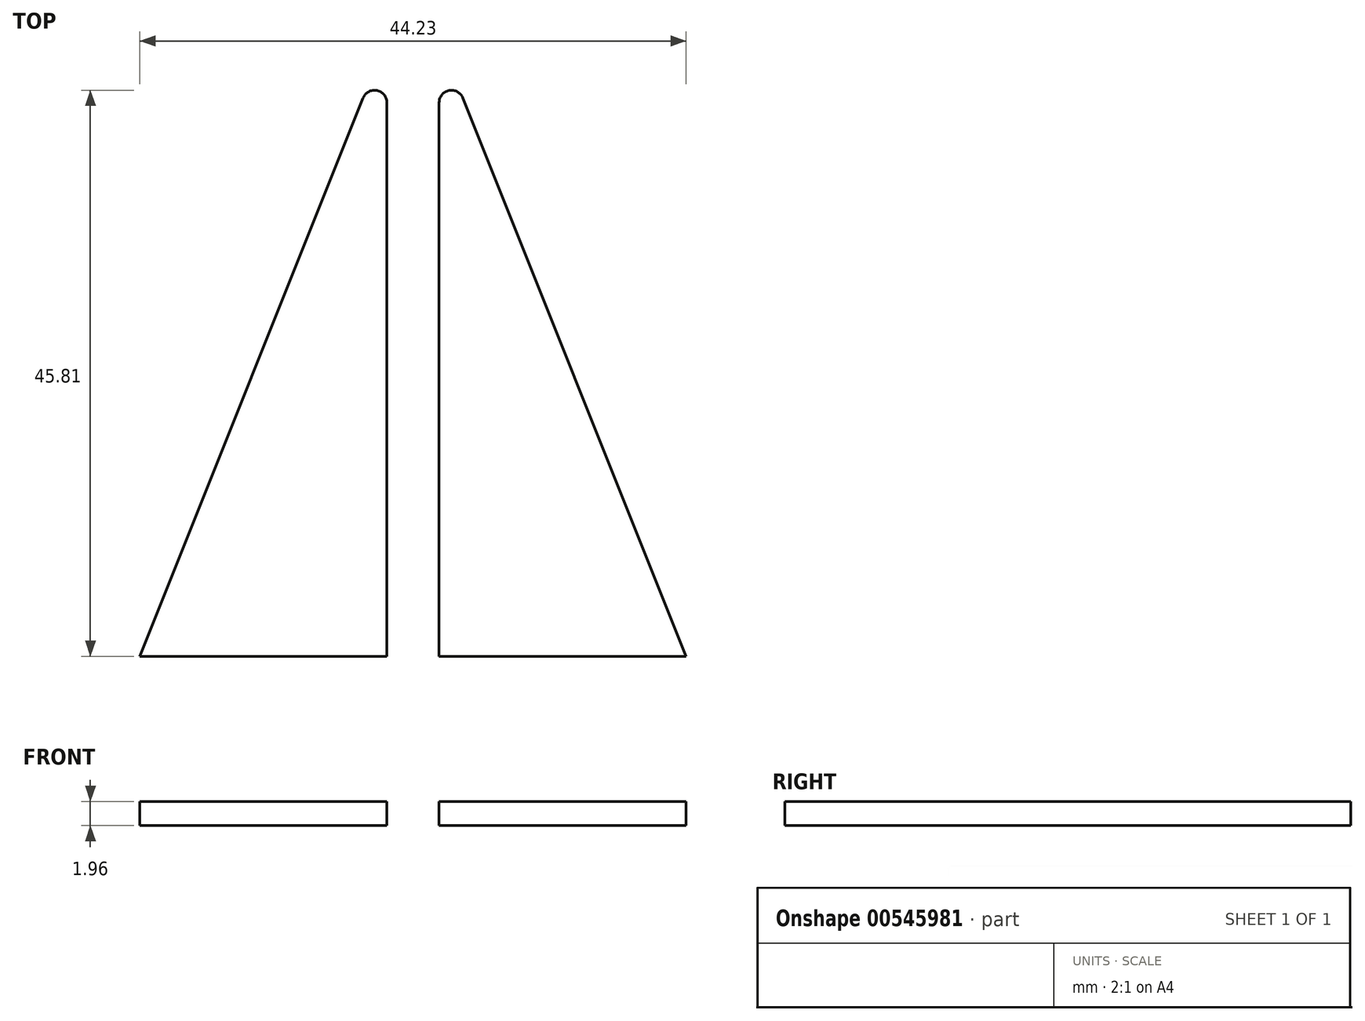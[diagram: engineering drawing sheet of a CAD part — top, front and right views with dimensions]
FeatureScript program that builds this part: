
annotation { "Feature Type Name" : "Feature", "Feature Type Description" : "" }
export const myFeature = defineFeature(function(context is Context, id is Id, definition is map)
    precondition{}
    {
        {
            var Q0;
            Q0=qCreatedBy(makeId("Top.planeOp"),FACE);
            var sketch = newSketch(context, id + "F0", { "sketchPlane" : qUnion([Q0])});
            skLineSegment(sketch, "E0", {"start": v(-10, 0) * mm, "end": v(10, 0) * mm});
            skLineSegment(sketch, "E1", {"start": v(10, 0) * mm, "end": v(10, 50) * mm});
            skLineSegment(sketch, "E2", {"start": v(-10, 0) * mm, "end": v(10, 50) * mm});
            skLineSegment(sketch, "E3", {"start": v(47.11, 43.1) * mm, "end": v(47.11, -24.25) * mm});
            skLineSegment(sketch, "E4.MirrorCS", {"start": v(104.23, 0) * mm, "end": v(84.23, 50) * mm});
            skLineSegment(sketch, "E5.MirrorCS", {"start": v(84.23, 0) * mm, "end": v(84.23, 50) * mm});
            skLineSegment(sketch, "E6.MirrorCS", {"start": v(104.23, 0) * mm, "end": v(84.23, 0) * mm});
            skSolve(sketch);
        }
        {
            var Q0;
            Q0=makeQuery(id+"F0.imprint","IMPRINT",FACE,{"disambiguationData":[TD([[makeQuery(id+"F0.imprint","IMPRINT",EDGE,{"derivedFrom":sQuery(id+"F0.wireOp",EDGE,"E4.MirrorCS")}),1.0]])]});
            var Q1;
            Q1=makeQuery(id+"F0.imprint","IMPRINT",FACE,{"disambiguationData":[TD([[makeQuery(id+"F0.imprint","IMPRINT",EDGE,{"derivedFrom":sQuery(id+"F0.wireOp",EDGE,"E0")}),1.0]])]});
            extrude(context, id + "F1", {"entities" : qUnion([Q0, Q1]), "depth" : 1.96 * mm, "offsetDistance" : 25 * mm});
        }
        {
            var Q0;
            Q0=makeQuery(id+"F1.opExtrude","SWEPT_EDGE",EDGE,{"disambiguationData":[OSD([sQuery(id+"F0.wireOp",EDGE,"E1"),sQuery(id+"F0.wireOp",EDGE,"E2")])]});
            var Q1;
            Q1=makeQuery(id+"F1.opExtrude","SWEPT_EDGE",EDGE,{"disambiguationData":[OSD([sQuery(id+"F0.wireOp",EDGE,"E4.MirrorCS"),sQuery(id+"F0.wireOp",EDGE,"E5.MirrorCS")])]});
            fillet(context, id + "F2", {"entities" : qUnion([Q0, Q1]), "radius" : 1 * mm, "tangentPropagation" : true, "allowEdgeOverflow" : false});
        }
        {
            var Q0;
            Q0=makeQuery(id+"F1.opExtrude","SWEPT_BODY",BODY,{"disambiguationData":[OSD([sQuery(id+"F0.wireOp",EDGE,"E4.MirrorCS"),sQuery(id+"F0.wireOp",EDGE,"E5.MirrorCS"),sQuery(id+"F0.wireOp",EDGE,"E6.MirrorCS")])]});
            var Q1;
            Q1=makeQuery(id+"F1.opExtrude","CAP_EDGE",EDGE,{"disambiguationData":[OSD([sQuery(id+"F0.wireOp",EDGE,"E6.MirrorCS")])],"isStart":false});
            var Q2;
            Q2=makeQuery(id+"F1.opExtrude","CAP_EDGE",EDGE,{"disambiguationData":[OSD([sQuery(id+"F0.wireOp",EDGE,"E6.MirrorCS")])],"isStart":false});
            transform(context, id + "F3", {"entities" : qUnion([Q0]), "transformType" : TransformType.TRANSLATION_DISTANCE, "transformDirection" : qUnion([Q2]), "distance" : 70 * mm, "makeCopy" : false});
        }
    });
